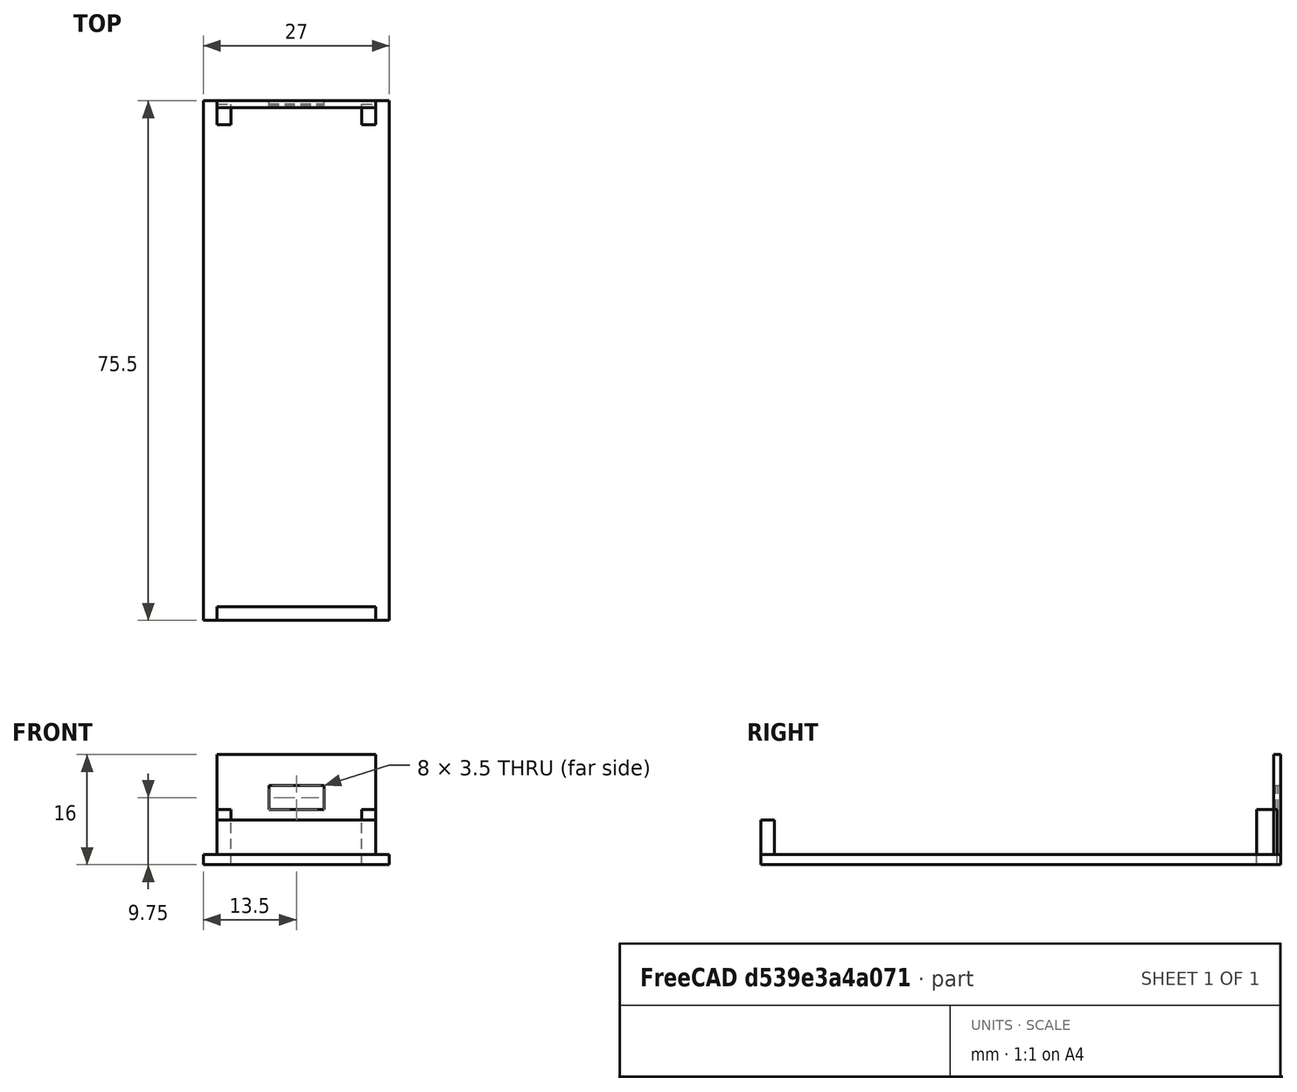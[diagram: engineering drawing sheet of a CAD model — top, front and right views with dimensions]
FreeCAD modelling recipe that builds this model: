
FCSTD DOCUMENT  (FreeCAD 0.20R29177 (Git))
Label: Anlogic FPGA programer top
License: All rights reserved
LicenseURL: http://en.wikipedia.org/wiki/All_rights_reserved
objects: Part::Box×7, Part::Cut×1
note: 8 computed .brp shape members not serialized (recipe doc carries the construction recipe); baked Part::Feature solids carry a one-line shape summary decoded from their .brp

FEATURE [Part::Box] Box  label="Kocka"
  AttacherType = Attacher::AttachEngine3D
  Height = 1.5
  Length = 27
  Width = 75.5
FEATURE [Part::Box] Box001  label="Kocka001"
  AttacherType = Attacher::AttachEngine3D
  Height = 5
  Length = 23
  Placement = pos=(2,0,1.5) rot=(0,0,1;0rad)
  Width = 2
FEATURE [Part::Box] Box002  label="Kocka002"
  AttacherType = Attacher::AttachEngine3D
  Height = 14.5
  Length = 23
  Placement = pos=(2,74.5,1.5) rot=(0,0,1;0rad)
  Width = 1
FEATURE [Part::Box] Box003  label="Kocka003"
  AttacherType = Attacher::AttachEngine3D
  Height = 3.5
  Length = 8
  Placement = pos=(9.5,74.5,8) rot=(0,0,1;0rad)
  Width = 1
FEATURE [Part::Cut] Cut
  Base = -> Box002
  Tool = -> Box003
FEATURE [Part::Box] Box004  label="Kocka004"
  AttacherType = Attacher::AttachEngine3D
  Height = 3.5
  Length = 8
  Placement = pos=(9.5,74.8,8) rot=(0,0,1;0rad)
  Width = 0.3
FEATURE [Part::Box] Box005  label="Kocka005"
  AttacherType = Attacher::AttachEngine3D
  Height = 8
  Length = 2
  Placement = pos=(2,72,0) rot=(0,0,1;0rad)
  Width = 3
FEATURE [Part::Box] Box006  label="Kocka006"
  AttacherType = Attacher::AttachEngine3D
  Height = 8
  Length = 2
  Placement = pos=(23,72,0) rot=(0,0,1;0rad)
  Width = 3
